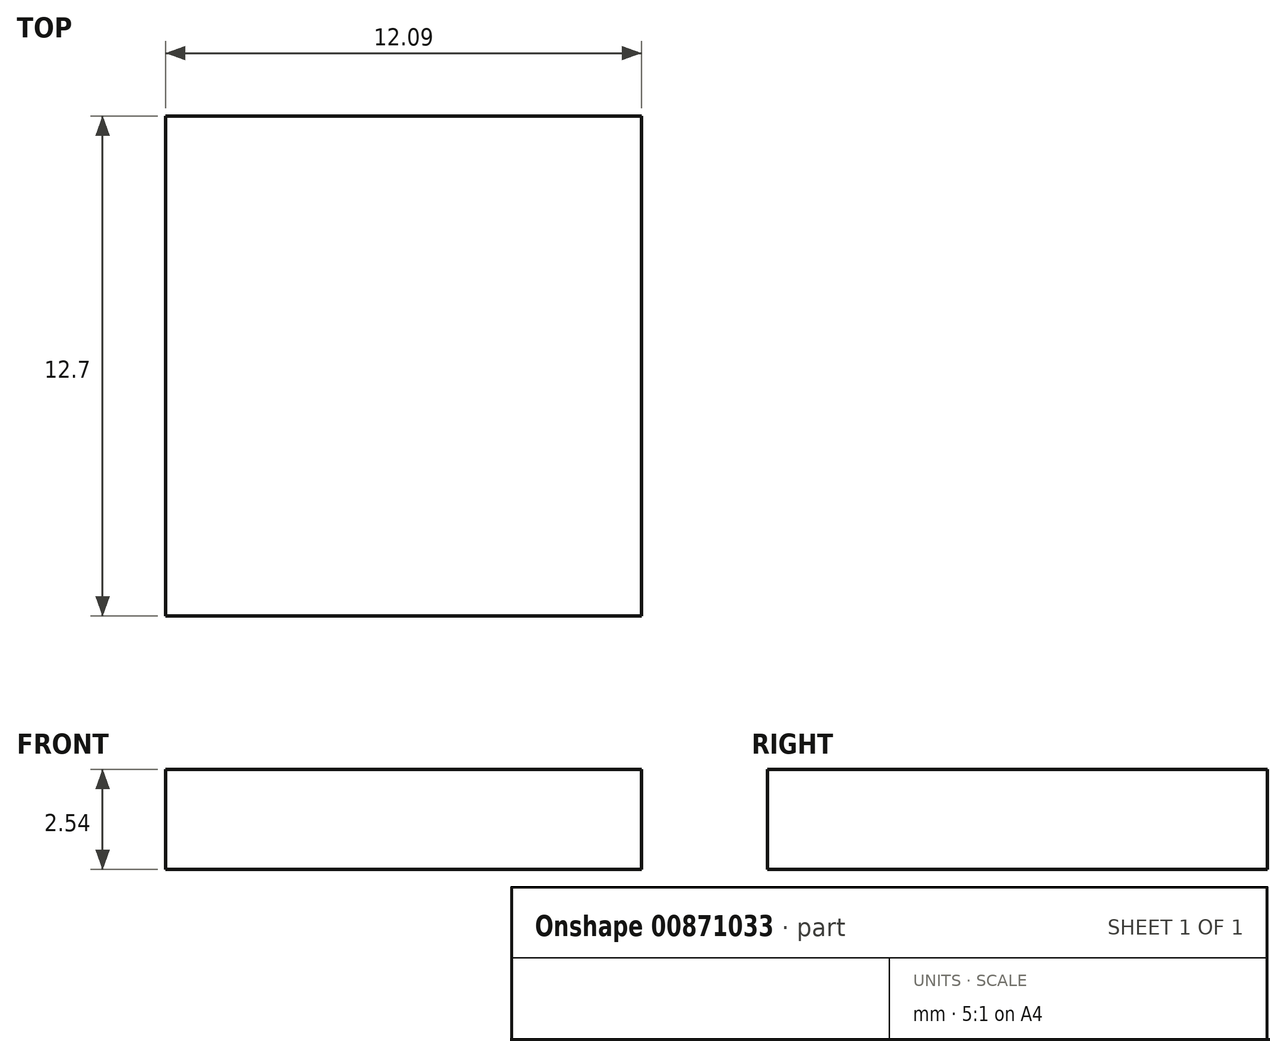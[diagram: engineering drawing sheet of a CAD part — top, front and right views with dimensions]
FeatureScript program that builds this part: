
annotation { "Feature Type Name" : "Feature", "Feature Type Description" : "" }
export const myFeature = defineFeature(function(context is Context, id is Id, definition is map)
    precondition{}
    {
        {
            var Q0;
            Q0=qCreatedBy(makeId("Top.planeOp"),FACE);
            var sketch = newSketch(context, id + "F0", { "sketchPlane" : qUnion([Q0])});
            skLineSegment(sketch, "E0.bottom", {"start": v(0, 0) * mm, "end": v(12.1, 0) * mm});
            skLineSegment(sketch, "E0.top", {"start": v(0, -12.7) * mm, "end": v(12.1, -12.7) * mm});
            skLineSegment(sketch, "E0.left", {"start": v(0, 0) * mm, "end": v(0, -12.7) * mm});
            skLineSegment(sketch, "E0.right", {"start": v(12.1, 0) * mm, "end": v(12.1, -12.7) * mm});
            skSolve(sketch);
        }
        {
            var Q0;
            Q0 = qSketchRegion(id + "F0", true);
            extrude(context, id + "F1", {"entities" : qUnion([Q0]), "oppositeDirection" : true, "depth" : 2.54 * mm, "offsetDistance" : 25.4 * mm});
        }
    });
